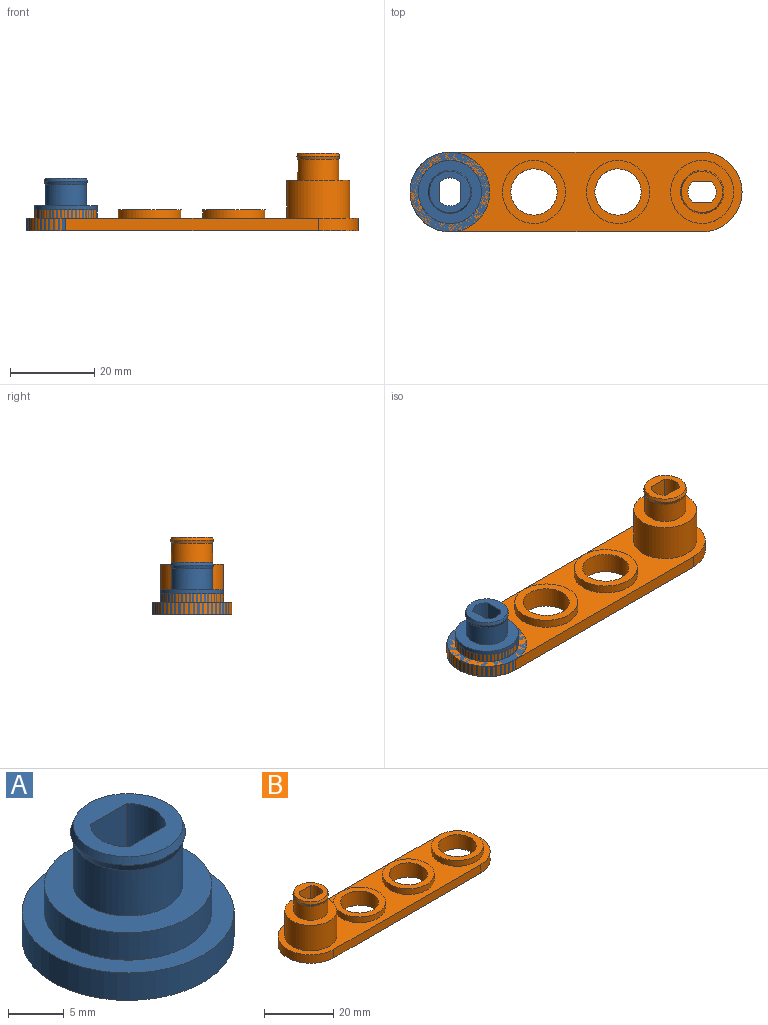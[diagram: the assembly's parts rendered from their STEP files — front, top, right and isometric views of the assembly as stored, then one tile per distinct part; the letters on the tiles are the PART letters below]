
ASSEMBLY  parts=2 mates=1
PART A: 13 faces, bbox 19x19x12.5 mm
  f0: cylinder r=3.35mm len=12.5mm, axis (0,0,-1), area 68.7mm2, adj f1,f4,f6,f10
  f1: plane 12.5x4.57mm, normal (0,1,0), area 57.1mm2, adj f0,f2,f6,f10
  f2: cylinder r=3.35mm len=12.5mm, axis (0,0,-1), area 68.7mm2, adj f1,f4,f6,f10
  f3: cylinder r=9.5mm len=19mm, axis (0,0,-1), area 179.1mm2, adj f5,f6
  f4: plane 12.5x4.57mm, normal (0,-1,0), area 57.1mm2, adj f0,f2,f6,f10
  f5: plane 19x19mm, normal (0,0,1), area 106.8mm2, adj f3,f7
  f6: plane 19x19mm, normal (0,0,-1), area 253.9mm2, adj f0,f1,f2,f3,f4
  f7: cylinder r=7.5mm len=15mm, axis (0,0,-1), area 141.4mm2, adj f5,f8
  f8: plane 15x15mm, normal (0,0,1), area 101.3mm2, adj f7,f9
  f9: cylinder r=4.9mm len=9.8mm, axis (0,0,-1), area 153.9mm2, adj f8,f11
  f10: plane 9.8x9.8mm, normal (0,0,1), area 45.8mm2, adj f0,f1,f2,f4,f12
  f11: cone r=5.15mm half-angle=18.4deg, axis (0,0,1), area 25mm2, adj f9,f12
  f12: cone r=4.9mm half-angle=18.4deg, axis (0,0,-1), area 25mm2, adj f10,f11
PART B: 25 faces, bbox 79x19x18.5 mm
  f0: cylinder r=9.5mm len=19mm, axis (0,0,-1), area 89.5mm2, adj f1,f5,f7,f8
  f1: plane 60x3mm, normal (0,-1,0), area 180mm2, adj f0,f2,f7,f8
  f2: cylinder r=9.5mm len=19mm, axis (0,0,-1), area 89.5mm2, adj f1,f5,f7,f8
  f3: cylinder r=5.5mm len=11mm, axis (0,0,-1), area 172.8mm2, adj f8,f13
  f4: cylinder r=5.5mm len=11mm, axis (0,0,-1), area 172.8mm2, adj f8,f11
  f5: plane 60x3mm, normal (0,1,0), area 180mm2, adj f0,f2,f7,f8
  f6: cylinder r=5.5mm len=11mm, axis (0,0,-1), area 172.8mm2, adj f8,f15
  f7: plane 79x19mm, normal (0,0,1), area 716.7mm2, adj f0,f1,f2,f5,f9,f10,f12,f14
  f8: plane 79x19mm, normal (0,0,-1), area 1108.8mm2, adj f0,f1,f2,f3,f4,f5,f6,f16
  f9: cylinder r=7.5mm len=15mm, axis (0,0,-1), area 424.1mm2, adj f7,f20
  f10: cylinder r=7.5mm len=15mm, axis (0,0,-1), area 94.2mm2, adj f7,f11
  f11: plane 15x15mm, normal (0,0,1), area 81.7mm2, adj f4,f10
  f12: cylinder r=7.5mm len=15mm, axis (0,0,-1), area 94.2mm2, adj f7,f13
  f13: plane 15x15mm, normal (0,0,1), area 81.7mm2, adj f3,f12
  f14: cylinder r=7.5mm len=15mm, axis (0,0,-1), area 94.2mm2, adj f7,f15
  f15: plane 15x15mm, normal (0,0,1), area 81.7mm2, adj f6,f14
  f16: cylinder r=3.35mm len=18.5mm, axis (0,0,-1), area 101.7mm2, adj f8,f17,f19,f22
  f17: plane 18.5x4.57mm, normal (0,1,0), area 84.5mm2, adj f8,f16,f18,f22
  f18: cylinder r=3.35mm len=18.5mm, axis (0,0,-1), area 101.7mm2, adj f8,f17,f19,f22
  f19: plane 18.5x4.57mm, normal (0,-1,0), area 84.5mm2, adj f8,f16,f18,f22
  f20: plane 15x15mm, normal (0,0,1), area 101.3mm2, adj f9,f21
  f21: cylinder r=4.9mm len=9.8mm, axis (0,0,-1), area 153.9mm2, adj f20,f23
  f22: plane 9.8x9.8mm, normal (0,0,1), area 45.8mm2, adj f16,f17,f18,f19,f24
  f23: cone r=5.15mm half-angle=18.4deg, axis (0,0,1), area 25mm2, adj f21,f24
  f24: cone r=4.9mm half-angle=18.4deg, axis (0,0,-1), area 25mm2, adj f22,f23
PLACE A rot(axis=(0,0,1),90deg) t=(0,0,0)mm
PLACE B rot(axis=(0,0,1),180deg) t=(60,0,0)mm
MATE fastened B.f2 <-> A.f0  axis (0,0,-1) through (0,0,0)mm
